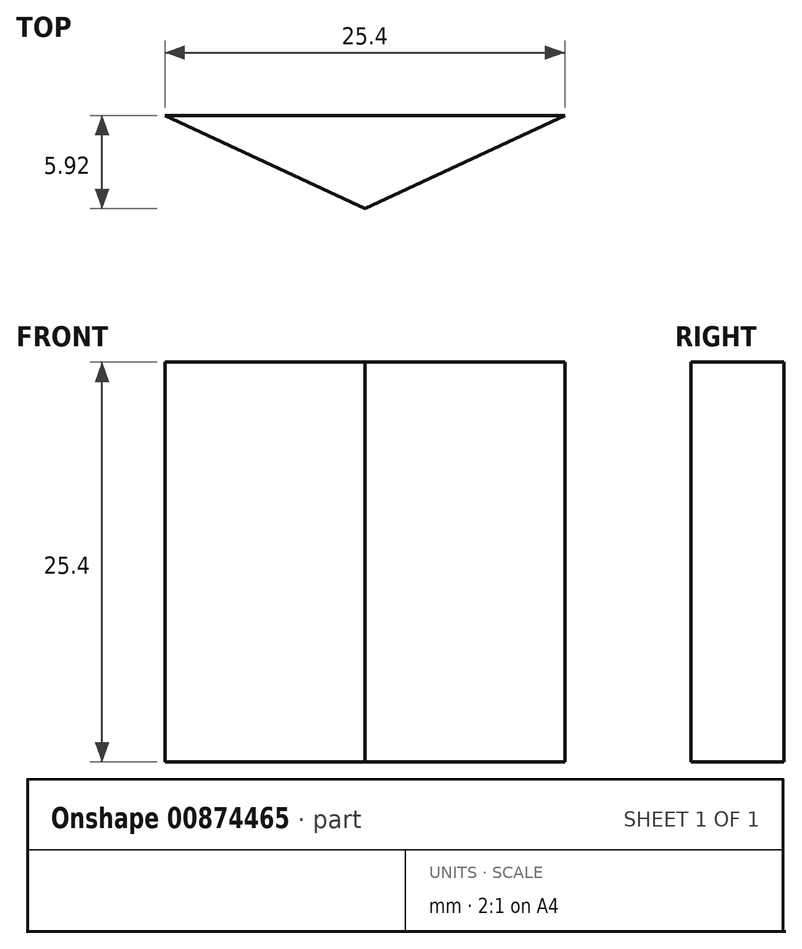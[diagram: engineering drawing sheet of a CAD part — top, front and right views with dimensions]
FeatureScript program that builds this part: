
annotation { "Feature Type Name" : "Feature", "Feature Type Description" : "" }
export const myFeature = defineFeature(function(context is Context, id is Id, definition is map)
    precondition{}
    {
        {
            var Q0;
            Q0=qCreatedBy(makeId("Top.planeOp"),FACE);
            var sketch = newSketch(context, id + "F0", { "sketchPlane" : qUnion([Q0])});
            skLineSegment(sketch, "E0", {"start": v(0, 0) * mm, "end": v(12.7, 5.92) * mm});
            skLineSegment(sketch, "E1", {"start": v(12.7, 5.92) * mm, "end": v(-12.7, 5.92) * mm});
            skLineSegment(sketch, "E2", {"start": v(-12.7, 5.92) * mm, "end": v(0, 0) * mm});
            skSolve(sketch);
        }
        {
            var Q0;
            Q0=makeQuery(id+"F0.imprint","IMPRINT",FACE,{"disambiguationData":[TD([[makeQuery(id+"F0.imprint","IMPRINT",EDGE,{"derivedFrom":sQuery(id+"F0.wireOp",EDGE,"E0")}),1.0]])]});
            extrude(context, id + "F1", {"entities" : qUnion([Q0]), "depth" : 25.4 * mm, "offsetDistance" : 25.4 * mm});
        }
    });
